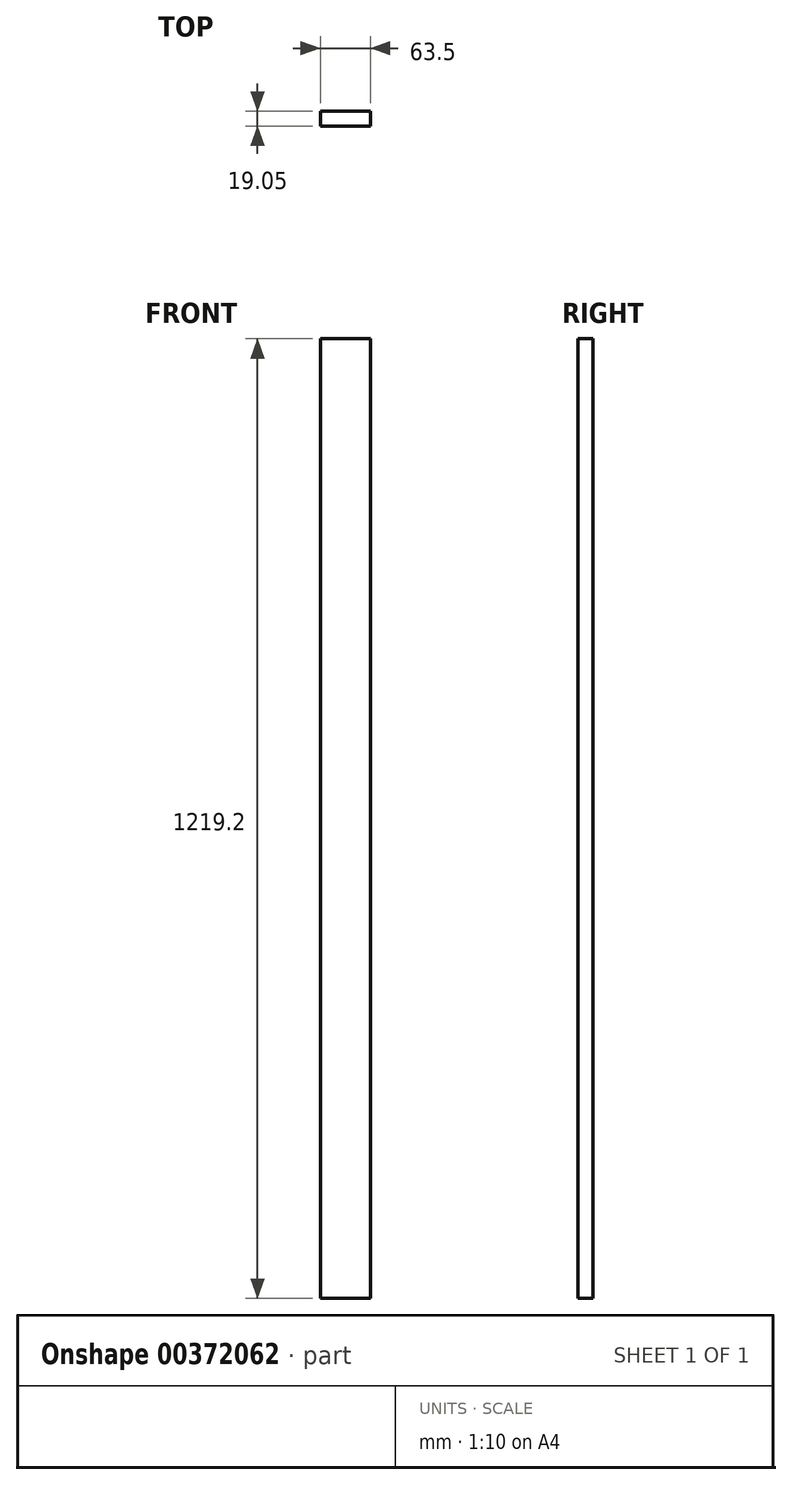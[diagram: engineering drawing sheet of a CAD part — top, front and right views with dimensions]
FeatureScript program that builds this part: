
annotation { "Feature Type Name" : "Feature", "Feature Type Description" : "" }
export const myFeature = defineFeature(function(context is Context, id is Id, definition is map)
    precondition{}
    {
        {
            var Q0;
            Q0=qCreatedBy(makeId("Front.planeOp"),FACE);
            var sketch = newSketch(context, id + "F0", { "sketchPlane" : qUnion([Q0])});
            skLineSegment(sketch, "E0.bottom", {"start": v(0, 0) * mm, "end": v(63.5, 0) * mm});
            skLineSegment(sketch, "E0.top", {"start": v(0, 1219.2) * mm, "end": v(63.5, 1219.2) * mm});
            skLineSegment(sketch, "E0.left", {"start": v(0, 0) * mm, "end": v(0, 1219.2) * mm});
            skLineSegment(sketch, "E0.right", {"start": v(63.5, 0) * mm, "end": v(63.5, 1219.2) * mm});
            skSolve(sketch);
        }
        {
            var Q0;
            Q0=makeQuery(id+"F0.imprint","IMPRINT",FACE,{"disambiguationData":[TD([[makeQuery(id+"F0.imprint","IMPRINT",EDGE,{"derivedFrom":sQuery(id+"F0.wireOp",EDGE,"E0.bottom")}),1.0]])]});
            extrude(context, id + "F1", {"entities" : qUnion([Q0]), "oppositeDirection" : true, "depth" : 19.05 * mm});
        }
    });
